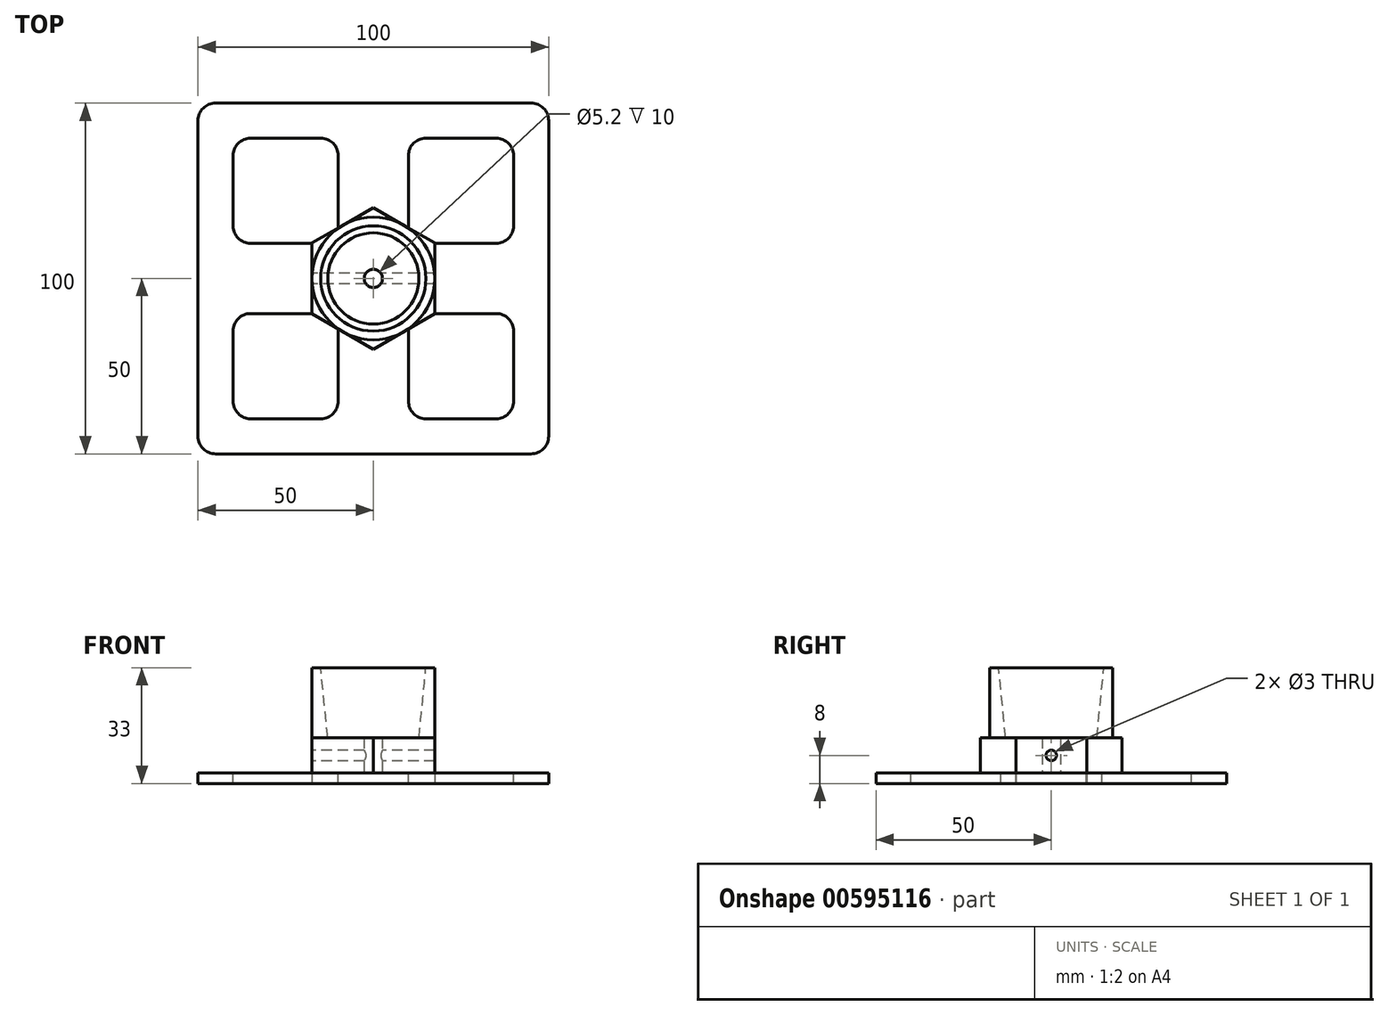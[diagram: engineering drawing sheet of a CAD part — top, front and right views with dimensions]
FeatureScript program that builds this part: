
annotation { "Feature Type Name" : "Feature", "Feature Type Description" : "" }
export const myFeature = defineFeature(function(context is Context, id is Id, definition is map)
    precondition{}
    {
        {
            var Q0;
            Q0=qCreatedBy(makeId("Top.planeOp"),FACE);
            var sketch = newSketch(context, id + "F0", { "sketchPlane" : qUnion([Q0])});
            skCircle(sketch, "E0", {"center": v(0, 0) * mm, "radius": 2.6 * mm});
            skCircle(sketch, "E1", {"center": v(0, 0) * mm, "radius": 17.5 * mm});
            skCircle(sketch, "E2.cCircle", {"center": v(0, 0) * mm, "radius": 17.5 * mm, "construction": true});
            skLineSegment(sketch, "E2.0", {"start": v(17.5, 10.1) * mm, "end": v(17.5, -10.1) * mm});
            skLineSegment(sketch, "E2.1", {"start": v(17.5, -10.1) * mm, "end": v(0, -20.2) * mm});
            skLineSegment(sketch, "E2.2", {"start": v(0, -20.2) * mm, "end": v(-17.5, -10.1) * mm});
            skLineSegment(sketch, "E2.3", {"start": v(-17.5, -10.1) * mm, "end": v(-17.5, 10.1) * mm});
            skLineSegment(sketch, "E2.4", {"start": v(-17.5, 10.1) * mm, "end": v(0, 20.2) * mm});
            skLineSegment(sketch, "E2.5", {"start": v(0, 20.2) * mm, "end": v(17.5, 10.1) * mm});
            skPoint(sketch, "E2.0.midPoint", {"position": v(17.5, 0) * mm});
            skSolve(sketch);
        }
        {
            var Q0;
            Q0=makeQuery(id+"F0.imprint","IMPRINT",FACE,{"disambiguationData":[TD([[makeQuery(id+"F0.imprint","IMPRINT",EDGE,{"derivedFrom":sQuery(id+"F0.wireOp",EDGE,"E0")}),-1.0]])]});
            var Q1;
            {var subQ0=sQuery(id+"F0.wireOp",EDGE,"E2.3");var subQ1=sQuery(id+"F0.wireOp",EDGE,"E1");var subQ2=makeQuery(id+"F0.imprint","INTERSECT",VERTEX,{"derivedFrom":[subQ1,subQ0]});Q1=makeQuery(id+"F0.imprint","IMPRINT",FACE,{"disambiguationData":[TD([[makeQuery(id+"F0.imprint","IMPRINT",EDGE,{"disambiguationData":[TD([[subQ2,-1.0]])],"derivedFrom":subQ1}),-1.0]])]});}
            var Q2;
            {var subQ0=sQuery(id+"F0.wireOp",EDGE,"E2.2");var subQ1=sQuery(id+"F0.wireOp",EDGE,"E1");var subQ2=makeQuery(id+"F0.imprint","INTERSECT",VERTEX,{"derivedFrom":[subQ1,subQ0]});Q2=makeQuery(id+"F0.imprint","IMPRINT",FACE,{"disambiguationData":[TD([[makeQuery(id+"F0.imprint","IMPRINT",EDGE,{"disambiguationData":[TD([[subQ2,-1.0]])],"derivedFrom":subQ1}),-1.0]])]});}
            var Q3;
            {var subQ0=sQuery(id+"F0.wireOp",EDGE,"E2.0");var subQ1=sQuery(id+"F0.wireOp",EDGE,"E1");var subQ2=makeQuery(id+"F0.imprint","INTERSECT",VERTEX,{"derivedFrom":[subQ1,subQ0]});Q3=makeQuery(id+"F0.imprint","IMPRINT",FACE,{"disambiguationData":[TD([[makeQuery(id+"F0.imprint","IMPRINT",EDGE,{"disambiguationData":[TD([[subQ2,1.0]])],"derivedFrom":subQ1}),-1.0]])]});}
            var Q4;
            {var subQ0=sQuery(id+"F0.wireOp",EDGE,"E2.5");var subQ1=sQuery(id+"F0.wireOp",EDGE,"E1");var subQ2=makeQuery(id+"F0.imprint","INTERSECT",VERTEX,{"derivedFrom":[subQ1,subQ0]});Q4=makeQuery(id+"F0.imprint","IMPRINT",FACE,{"disambiguationData":[TD([[makeQuery(id+"F0.imprint","IMPRINT",EDGE,{"disambiguationData":[TD([[subQ2,1.0]])],"derivedFrom":subQ1}),-1.0]])]});}
            var Q5;
            {var subQ0=sQuery(id+"F0.wireOp",EDGE,"E2.5");var subQ1=sQuery(id+"F0.wireOp",EDGE,"E1");var subQ2=makeQuery(id+"F0.imprint","INTERSECT",VERTEX,{"derivedFrom":[subQ1,subQ0]});Q5=makeQuery(id+"F0.imprint","IMPRINT",FACE,{"disambiguationData":[TD([[makeQuery(id+"F0.imprint","IMPRINT",EDGE,{"disambiguationData":[TD([[subQ2,-1.0]])],"derivedFrom":subQ1}),-1.0]])]});}
            var Q6;
            {var subQ0=sQuery(id+"F0.wireOp",EDGE,"E2.4");var subQ1=sQuery(id+"F0.wireOp",EDGE,"E1");var subQ2=makeQuery(id+"F0.imprint","INTERSECT",VERTEX,{"derivedFrom":[subQ1,subQ0]});Q6=makeQuery(id+"F0.imprint","IMPRINT",FACE,{"disambiguationData":[TD([[makeQuery(id+"F0.imprint","IMPRINT",EDGE,{"disambiguationData":[TD([[subQ2,-1.0]])],"derivedFrom":subQ1}),-1.0]])]});}
            extrude(context, id + "F1", {"entities" : qUnion([Q0, Q1, Q2, Q3, Q4, Q5, Q6]), "depth" : 10 * mm, "offsetDistance" : 25 * mm});
        }
        {
            var Q0;
            Q0=makeQuery(id+"F1.opExtrude","CAP_FACE",FACE,{"disambiguationData":[OSD([sQuery(id+"F0.wireOp",EDGE,"E0"),sQuery(id+"F0.wireOp",EDGE,"E1")])],"isStart":false});
            var sketch = newSketch(context, id + "F2", { "sketchPlane" : qUnion([Q0])});
            skCircle(sketch, "E3", {"center": v(0, 0) * mm, "radius": 14 * mm});
            skCircle(sketch, "E4", {"center": v(0, 0) * mm, "radius": 17.5 * mm});
            skSolve(sketch);
        }
        {
            var Q0;
            Q0=makeQuery(id+"F2.imprint","IMPRINT",FACE,{"disambiguationData":[TD([[makeQuery(id+"F2.imprint","IMPRINT",EDGE,{"derivedFrom":sQuery(id+"F2.wireOp",EDGE,"E3")}),-1.0]])]});
            extrude(context, id + "F3", {"entities" : qUnion([Q0]), "operationType" : NewBodyOperationType.ADD, "depth" : 20 * mm, "offsetDistance" : 25 * mm});
        }
        {
            var Q0;
            Q0=makeQuery(id+"F1.opExtrude","SWEPT_FACE",FACE,{"disambiguationData":[OSD([sQuery(id+"F0.wireOp",EDGE,"E2.3")])]});
            var sketch = newSketch(context, id + "F4", { "sketchPlane" : qUnion([Q0])});
            skCircle(sketch, "E5", {"center": v(0, 5) * mm, "radius": 1.5 * mm});
            skSolve(sketch);
        }
        {
            var Q0;
            Q0=makeQuery(id+"F4.imprint","IMPRINT",FACE,{"disambiguationData":[TD([[makeQuery(id+"F4.imprint","IMPRINT",EDGE,{"derivedFrom":sQuery(id+"F4.wireOp",EDGE,"E5")}),1.0]])]});
            extrude(context, id + "F5", {"entities" : qUnion([Q0]), "operationType" : NewBodyOperationType.REMOVE, "endBound" : BoundingType.THROUGH_ALL, "oppositeDirection" : true, "depth" : 25 * mm, "offsetDistance" : 25 * mm});
        }
        {
            var Q0;
            Q0=makeQuery(id+"F3.opExtrude","SWEPT_FACE",FACE,{"disambiguationData":[OSD([sQuery(id+"F2.wireOp",EDGE,"E3")])]});
            chamfer(context, id + "F6", {"entities" : qUnion([Q0]), "chamferType" : ChamferType.TWO_OFFSETS, "width1" : 10 * mm, "oppositeDirection" : false, "width2" : 1 * mm});
        }
        {
            var Q0;
            Q0=qCreatedBy(makeId("Top.planeOp"),FACE);
            var sketch = newSketch(context, id + "F7", { "sketchPlane" : qUnion([Q0])});
            skLineSegment(sketch, "E6.bottom", {"start": v(50, -50) * mm, "end": v(-50, -50) * mm});
            skLineSegment(sketch, "E6.top", {"start": v(50, 50) * mm, "end": v(-50, 50) * mm});
            skLineSegment(sketch, "E6.left", {"start": v(50, -50) * mm, "end": v(50, 50) * mm});
            skLineSegment(sketch, "E6.right", {"start": v(-50, -50) * mm, "end": v(-50, 50) * mm});
            skPoint(sketch, "E6.middle", {"position": v(0, 0) * mm});
            skSolve(sketch);
        }
        {
            var Q0;
            Q0=makeQuery(id+"F7.imprint","IMPRINT",FACE,{"disambiguationData":[TD([[makeQuery(id+"F7.imprint","IMPRINT",EDGE,{"derivedFrom":sQuery(id+"F7.wireOp",EDGE,"E6.bottom")}),-1.0]])]});
            extrude(context, id + "F8", {"entities" : qUnion([Q0]), "operationType" : NewBodyOperationType.ADD, "oppositeDirection" : true, "depth" : 3 * mm, "offsetDistance" : 25 * mm});
        }
        {
            var Q0;
            {var subQ0=sQuery(id+"F7.wireOp",EDGE,"E6.bottom");var subQ1=sQuery(id+"F7.wireOp",EDGE,"E6.top");var subQ2=sQuery(id+"F7.wireOp",EDGE,"E6.left");var subQ3=sQuery(id+"F7.wireOp",EDGE,"E6.right");Q0=makeQuery(id+"F8.boolean.opBoolean","SPLIT",FACE,{"disambiguationData":[TD([makeQuery(id+"F1.opExtrude","SWEPT_FACE",FACE,{"disambiguationData":[OSD([sQuery(id+"F0.wireOp",EDGE,"E2.0")])]})])],"derivedFrom":makeQuery(id+"F8.opExtrude","CAP_FACE",FACE,{"disambiguationData":[OSD([subQ0,subQ1,subQ2,subQ3])],"isStart":true})});}
            var sketch = newSketch(context, id + "F9", { "sketchPlane" : qUnion([Q0])});
            skLineSegment(sketch, "E7.bottom", {"start": v(-40, -40) * mm, "end": v(40, -40) * mm});
            skLineSegment(sketch, "E7.top", {"start": v(-40, 40) * mm, "end": v(40, 40) * mm});
            skLineSegment(sketch, "E7.left", {"start": v(-40, -40) * mm, "end": v(-40, 40) * mm});
            skLineSegment(sketch, "E7.right", {"start": v(40, -40) * mm, "end": v(40, 40) * mm});
            skLineSegment(sketch, "E8", {"start": v(-10, 40) * mm, "end": v(-10, -40) * mm});
            skPoint(sketch, "E8.startSnap0", {"position": v(-10, 15.16) * mm});
            skLineSegment(sketch, "E9", {"start": v(10, 40) * mm, "end": v(10, -40) * mm});
            skLineSegment(sketch, "E10", {"start": v(-40, 10) * mm, "end": v(40, 10) * mm});
            skLineSegment(sketch, "E11", {"start": v(-40, -10) * mm, "end": v(40, -10) * mm});
            skSolve(sketch);
        }
        {
            var Q0;
            {var subQ1=sQuery(id+"F9.wireOp",EDGE,"E7.left");var subQ8=sQuery(id+"F9.wireOp",EDGE,"E7.top");var subQ11=makeQuery(id+"F9.imprint","INTERSECT",VERTEX,{"derivedFrom":[subQ8,subQ1]});Q0=makeQuery(id+"F9.imprint","IMPRINT",FACE,{"disambiguationData":[TD([[makeQuery(id+"F9.imprint","IMPRINT",EDGE,{"disambiguationData":[TD([[subQ11,-1.0]])],"derivedFrom":subQ8}),-1.0]])]});}
            var Q1;
            {var subQ1=sQuery(id+"F9.wireOp",EDGE,"E7.top");var subQ6=sQuery(id+"F9.wireOp",EDGE,"E7.right");var subQ11=makeQuery(id+"F9.imprint","INTERSECT",VERTEX,{"derivedFrom":[subQ1,subQ6]});Q1=makeQuery(id+"F9.imprint","IMPRINT",FACE,{"disambiguationData":[TD([[makeQuery(id+"F9.imprint","IMPRINT",EDGE,{"disambiguationData":[TD([[subQ11,1.0]])],"derivedFrom":subQ1}),-1.0]])]});}
            var Q2;
            {var subQ1=sQuery(id+"F9.wireOp",EDGE,"E7.right");var subQ5=sQuery(id+"F9.wireOp",EDGE,"E7.bottom");var subQ6=makeQuery(id+"F9.imprint","INTERSECT",VERTEX,{"derivedFrom":[subQ5,subQ1]});Q2=makeQuery(id+"F9.imprint","IMPRINT",FACE,{"disambiguationData":[TD([[makeQuery(id+"F9.imprint","IMPRINT",EDGE,{"disambiguationData":[TD([[subQ6,1.0]])],"derivedFrom":subQ5}),1.0]])]});}
            var Q3;
            {var subQ1=sQuery(id+"F9.wireOp",EDGE,"E7.left");var subQ6=sQuery(id+"F9.wireOp",EDGE,"E7.bottom");var subQ10=makeQuery(id+"F9.imprint","INTERSECT",VERTEX,{"derivedFrom":[subQ6,subQ1]});Q3=makeQuery(id+"F9.imprint","IMPRINT",FACE,{"disambiguationData":[TD([[makeQuery(id+"F9.imprint","IMPRINT",EDGE,{"disambiguationData":[TD([[subQ10,-1.0]])],"derivedFrom":subQ6}),1.0]])]});}
            extrude(context, id + "F10", {"entities" : qUnion([Q0, Q1, Q2, Q3]), "operationType" : NewBodyOperationType.REMOVE, "oppositeDirection" : true, "depth" : 25 * mm, "offsetDistance" : 25 * mm});
        }
        {
            var Q0;
            Q0=makeQuery(id+"F10.boolean.opBoolean","COPY",EDGE,{"derivedFrom":makeQuery(id+"F10.opExtrude","SWEPT_EDGE",EDGE,{"disambiguationData":[OSD([sQuery(id+"F9.wireOp",EDGE,"E7.top"),sQuery(id+"F9.wireOp",EDGE,"E7.left")])]})});
            var Q1;
            Q1=makeQuery(id+"F10.boolean.opBoolean","COPY",EDGE,{"derivedFrom":makeQuery(id+"F10.opExtrude","SWEPT_EDGE",EDGE,{"disambiguationData":[OSD([sQuery(id+"F9.wireOp",EDGE,"E7.top"),sQuery(id+"F9.wireOp",EDGE,"E8")])]})});
            var Q2;
            Q2=makeQuery(id+"F10.boolean.opBoolean","COPY",EDGE,{"derivedFrom":makeQuery(id+"F10.opExtrude","SWEPT_EDGE",EDGE,{"disambiguationData":[OSD([sQuery(id+"F9.wireOp",EDGE,"E7.left"),sQuery(id+"F9.wireOp",EDGE,"E10")])]})});
            var Q3;
            Q3=makeQuery(id+"F10.boolean.opBoolean","COPY",EDGE,{"derivedFrom":makeQuery(id+"F10.opExtrude","SWEPT_EDGE",EDGE,{"disambiguationData":[OSD([sQuery(id+"F9.wireOp",EDGE,"E7.top"),sQuery(id+"F9.wireOp",EDGE,"E9")])]})});
            var Q4;
            Q4=makeQuery(id+"F10.boolean.opBoolean","COPY",EDGE,{"derivedFrom":makeQuery(id+"F10.opExtrude","SWEPT_EDGE",EDGE,{"disambiguationData":[OSD([sQuery(id+"F9.wireOp",EDGE,"E7.top"),sQuery(id+"F9.wireOp",EDGE,"E7.right")])]})});
            var Q5;
            Q5=makeQuery(id+"F10.boolean.opBoolean","COPY",EDGE,{"derivedFrom":makeQuery(id+"F10.opExtrude","SWEPT_EDGE",EDGE,{"disambiguationData":[OSD([sQuery(id+"F9.wireOp",EDGE,"E7.right"),sQuery(id+"F9.wireOp",EDGE,"E10")])]})});
            var Q6;
            Q6=makeQuery(id+"F10.boolean.opBoolean","COPY",EDGE,{"derivedFrom":makeQuery(id+"F10.opExtrude","SWEPT_EDGE",EDGE,{"disambiguationData":[OSD([sQuery(id+"F9.wireOp",EDGE,"E7.right"),sQuery(id+"F9.wireOp",EDGE,"E11")])]})});
            var Q7;
            Q7=makeQuery(id+"F10.boolean.opBoolean","COPY",EDGE,{"derivedFrom":makeQuery(id+"F10.opExtrude","SWEPT_EDGE",EDGE,{"disambiguationData":[OSD([sQuery(id+"F9.wireOp",EDGE,"E7.bottom"),sQuery(id+"F9.wireOp",EDGE,"E9")])]})});
            var Q8;
            Q8=makeQuery(id+"F10.boolean.opBoolean","COPY",EDGE,{"derivedFrom":makeQuery(id+"F10.opExtrude","SWEPT_EDGE",EDGE,{"disambiguationData":[OSD([sQuery(id+"F9.wireOp",EDGE,"E7.bottom"),sQuery(id+"F9.wireOp",EDGE,"E7.right")])]})});
            var Q9;
            Q9=makeQuery(id+"F10.boolean.opBoolean","COPY",EDGE,{"derivedFrom":makeQuery(id+"F10.opExtrude","SWEPT_EDGE",EDGE,{"disambiguationData":[OSD([sQuery(id+"F9.wireOp",EDGE,"E7.bottom"),sQuery(id+"F9.wireOp",EDGE,"E8")])]})});
            var Q10;
            Q10=makeQuery(id+"F10.boolean.opBoolean","COPY",EDGE,{"derivedFrom":makeQuery(id+"F10.opExtrude","SWEPT_EDGE",EDGE,{"disambiguationData":[OSD([sQuery(id+"F9.wireOp",EDGE,"E7.bottom"),sQuery(id+"F9.wireOp",EDGE,"E7.left")])]})});
            var Q11;
            Q11=makeQuery(id+"F10.boolean.opBoolean","COPY",EDGE,{"derivedFrom":makeQuery(id+"F10.opExtrude","SWEPT_EDGE",EDGE,{"disambiguationData":[OSD([sQuery(id+"F9.wireOp",EDGE,"E7.left"),sQuery(id+"F9.wireOp",EDGE,"E11")])]})});
            var Q12;
            Q12=makeQuery(id+"F8.opExtrude","SWEPT_EDGE",EDGE,{"disambiguationData":[OSD([sQuery(id+"F7.wireOp",EDGE,"E6.bottom"),sQuery(id+"F7.wireOp",EDGE,"E6.left")])]});
            var Q13;
            Q13=makeQuery(id+"F8.opExtrude","SWEPT_EDGE",EDGE,{"disambiguationData":[OSD([sQuery(id+"F7.wireOp",EDGE,"E6.bottom"),sQuery(id+"F7.wireOp",EDGE,"E6.right")])]});
            var Q14;
            Q14=makeQuery(id+"F8.opExtrude","SWEPT_EDGE",EDGE,{"disambiguationData":[OSD([sQuery(id+"F7.wireOp",EDGE,"E6.top"),sQuery(id+"F7.wireOp",EDGE,"E6.right")])]});
            var Q15;
            Q15=makeQuery(id+"F8.opExtrude","SWEPT_EDGE",EDGE,{"disambiguationData":[OSD([sQuery(id+"F7.wireOp",EDGE,"E6.top"),sQuery(id+"F7.wireOp",EDGE,"E6.left")])]});
            fillet(context, id + "F11", {"entities" : qUnion([Q0, Q1, Q2, Q3, Q4, Q5, Q6, Q7, Q8, Q9, Q10, Q11, Q12, Q13, Q14, Q15]), "radius" : 5 * mm, "tangentPropagation" : true, "allowEdgeOverflow" : false});
        }
    });
